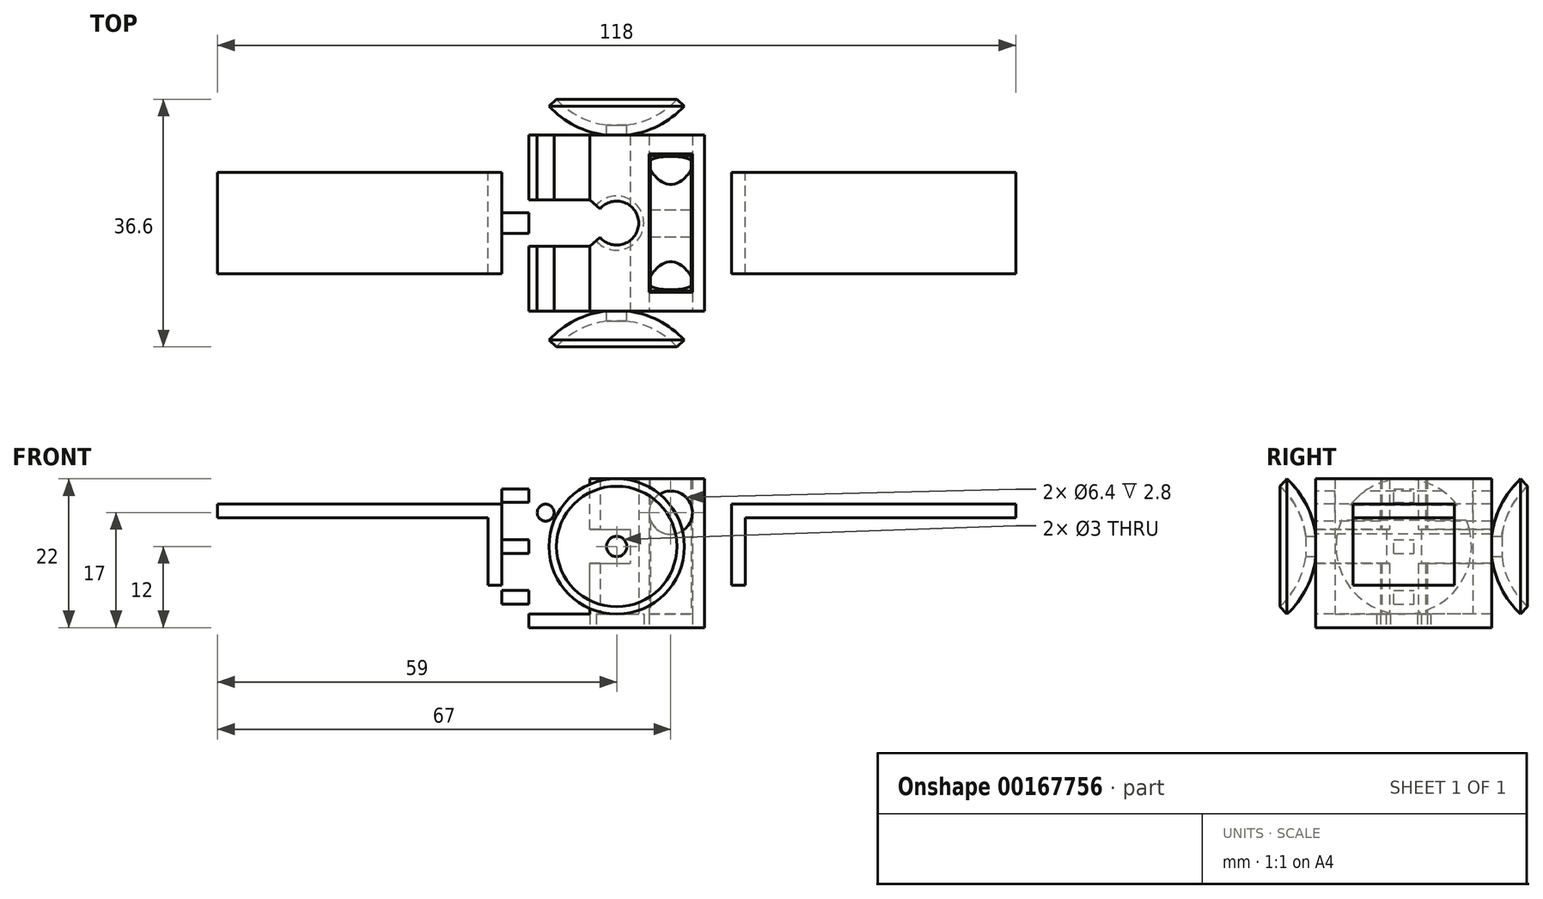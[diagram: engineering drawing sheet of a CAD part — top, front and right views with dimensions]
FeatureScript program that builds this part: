
annotation { "Feature Type Name" : "Feature", "Feature Type Description" : "" }
export const myFeature = defineFeature(function(context is Context, id is Id, definition is map)
    precondition{}
    {
        {
            assignVariable(context, id + "F0", {"name" : "e", "anyValue" : 15});
        }
        {
            var Q0;
            Q0=qCreatedBy(makeId("Front.planeOp"),FACE);
            var sketch = newSketch(context, id + "F1", { "sketchPlane" : qUnion([Q0])});
            skLineSegment(sketch, "E0.bottom", {"start": v(-4, 0) * mm, "end": v(-13, 0) * mm});
            skLineSegment(sketch, "E0.top", {"start": v(-4, 20) * mm, "end": v(-13, 20) * mm});
            skLineSegment(sketch, "E0.left", {"start": v(-4, 0) * mm, "end": v(-4, 20) * mm});
            skLineSegment(sketch, "E0.right", {"start": v(-13, 0) * mm, "end": v(-13, 20) * mm});
            skLineSegment(sketch, "E1.bottom", {"start": v(-4, 6.27) * mm, "end": v(-0.49, 6.27) * mm, "construction": true});
            skLineSegment(sketch, "E1.top", {"start": v(-4, 8.27) * mm, "end": v(-0.49, 8.27) * mm, "construction": true});
            skLineSegment(sketch, "E1.right", {"start": v(-0.49, 6.27) * mm, "end": v(-0.49, 8.27) * mm, "construction": true});
            skLineSegment(sketch, "E2", {"start": v(-4, 0) * mm, "end": v(18.43, 40.1) * mm, "construction": true});
            skLineSegment(sketch, "E3.bottom", {"start": v(-13, 18.5) * mm, "end": v(-17, 18.5) * mm});
            skLineSegment(sketch, "E3.top", {"start": v(-13, 16.5) * mm, "end": v(-17, 16.5) * mm});
            skLineSegment(sketch, "E3.left", {"start": v(-13, 18.5) * mm, "end": v(-13, 16.5) * mm});
            skLineSegment(sketch, "E3.right", {"start": v(-17, 18.5) * mm, "end": v(-17, 16.5) * mm});
            skLineSegment(sketch, "E4.bottom", {"start": v(-13, 11) * mm, "end": v(-17, 11) * mm});
            skLineSegment(sketch, "E4.top", {"start": v(-13, 9) * mm, "end": v(-17, 9) * mm});
            skLineSegment(sketch, "E4.left", {"start": v(-13, 11) * mm, "end": v(-13, 9) * mm});
            skLineSegment(sketch, "E4.right", {"start": v(-17, 11) * mm, "end": v(-17, 9) * mm});
            skLineSegment(sketch, "E5.bottom", {"start": v(-13, 1.5) * mm, "end": v(-17, 1.5) * mm});
            skLineSegment(sketch, "E5.top", {"start": v(-13, 3.5) * mm, "end": v(-17, 3.5) * mm});
            skLineSegment(sketch, "E5.left", {"start": v(-13, 1.5) * mm, "end": v(-13, 3.5) * mm});
            skLineSegment(sketch, "E5.right", {"start": v(-17, 1.5) * mm, "end": v(-17, 3.5) * mm});
            skLineSegment(sketch, "E6", {"start": v(-17, 10) * mm, "end": v(-4, 10) * mm, "construction": true});
            skCircle(sketch, "E7", {"center": v(-10.5, 5) * mm, "radius": 1.25 * mm});
            skLineSegment(sketch, "E8", {"start": v(-10.5, 15) * mm, "end": v(-10.5, 5) * mm, "construction": true});
            skCircle(sketch, "E9.MirrorC", {"center": v(-10.5, 15) * mm, "radius": 1.25 * mm});
            skLineSegment(sketch, "E10.bottom", {"start": v(-3, 0) * mm, "end": v(3, 0) * mm, "construction": true});
            skLineSegment(sketch, "E10.top", {"start": v(-3, 28.23) * mm, "end": v(3, 28.23) * mm, "construction": true});
            skLineSegment(sketch, "E10.left", {"start": v(-3, 0) * mm, "end": v(-3, 28.23) * mm, "construction": true});
            skLineSegment(sketch, "E10.right", {"start": v(3, 0) * mm, "end": v(3, 28.23) * mm, "construction": true});
            skSolve(sketch);
        }
        {
            var Q0;
            {var subQ5=sQuery(id+"F1.wireOp",EDGE,"E0.bottom");Q0=makeQuery(id+"F1.imprint","IMPRINT",FACE,{"disambiguationData":[TD([[makeQuery(id+"F1.imprint","IMPRINT",EDGE,{"derivedFrom":subQ5}),-1.0]])]});}
            extrude(context, id + "F2", {"entities" : qUnion([Q0]), "endBound" : BoundingType.SYMMETRIC, "depth" : 6.5 * mm, "offsetDistance" : 25 * mm});
        }
        {
            var Q0;
            Q0=makeQuery(id+"F1.imprint","IMPRINT",FACE,{"disambiguationData":[TD([[makeQuery(id+"F1.imprint","IMPRINT",EDGE,{"derivedFrom":sQuery(id+"F1.wireOp",EDGE,"E3.bottom")}),1.0]])]});
            var Q1;
            Q1=makeQuery(id+"F1.imprint","IMPRINT",FACE,{"disambiguationData":[TD([[makeQuery(id+"F1.imprint","IMPRINT",EDGE,{"derivedFrom":sQuery(id+"F1.wireOp",EDGE,"E4.bottom")}),1.0]])]});
            var Q2;
            Q2=makeQuery(id+"F1.imprint","IMPRINT",FACE,{"disambiguationData":[TD([[makeQuery(id+"F1.imprint","IMPRINT",EDGE,{"derivedFrom":sQuery(id+"F1.wireOp",EDGE,"E5.bottom")}),-1.0]])]});
            extrude(context, id + "F3", {"entities" : qUnion([Q0, Q1, Q2]), "endBound" : BoundingType.SYMMETRIC, "depth" : 3 * mm, "offsetDistance" : 25 * mm});
        }
        {
            var Q0;
            Q0=qCreatedBy(makeId("Right.planeOp"),FACE);
            var sketch = newSketch(context, id + "F4", { "sketchPlane" : qUnion([Q0])});
            skCircle(sketch, "E11", {"center": v(0, 10) * mm, "radius": 10 * mm});
            skSolve(sketch);
        }
        {
            var Q0;
            Q0 = qSketchRegion(id + "F4", true);
            extrude(context, id + "F5", {"entities" : qUnion([Q0]), "depth" : 11 * mm, "offsetDistance" : 25 * mm, "hasSecondDirection" : true, "secondDirectionOppositeDirection" : true, "secondDirectionDepth" : -5 * mm});
        }
        {
            var Q0;
            Q0=qCreatedBy(makeId("Top.planeOp"),FACE);
            var sketch = newSketch(context, id + "F6", { "sketchPlane" : qUnion([Q0])});
            skLineSegment(sketch, "E12", {"start": v(-13, 3.45) * mm, "end": v(-4, 3.45) * mm});
            skLineSegment(sketch, "E13", {"start": v(4.8, 0) * mm, "end": v(4.8, 10.2) * mm});
            skLineSegment(sketch, "E14", {"start": v(4.8, 10.2) * mm, "end": v(11.2, 10.2) * mm});
            skLineSegment(sketch, "E15", {"start": v(11.2, 10.2) * mm, "end": v(11.2, 0) * mm});
            skLineSegment(sketch, "E16", {"start": v(11.2, 0) * mm, "end": v(13, 0) * mm});
            skLineSegment(sketch, "E17", {"start": v(13, 0) * mm, "end": v(13, 13) * mm});
            skLineSegment(sketch, "E18", {"start": v(13, 13) * mm, "end": v(-13, 13) * mm});
            skLineSegment(sketch, "E19", {"start": v(-13, 13) * mm, "end": v(-13, 3.45) * mm});
            skLineSegment(sketch, "E20.MirrorCS", {"start": v(4.8, 0) * mm, "end": v(4.8, -10.2) * mm});
            skLineSegment(sketch, "E21.MirrorCS", {"start": v(-13, -3.45) * mm, "end": v(-4, -3.45) * mm});
            skLineSegment(sketch, "E22.MirrorCS", {"start": v(4.8, -10.2) * mm, "end": v(11.2, -10.2) * mm});
            skLineSegment(sketch, "E23.MirrorCS", {"start": v(13, 0) * mm, "end": v(13, -13) * mm});
            skLineSegment(sketch, "E24.MirrorCS", {"start": v(13, -13) * mm, "end": v(-13, -13) * mm});
            skLineSegment(sketch, "E25.MirrorCS", {"start": v(-13, -13) * mm, "end": v(-13, -3.45) * mm});
            skLineSegment(sketch, "E26.MirrorCS", {"start": v(11.2, -10.2) * mm, "end": v(11.2, 0) * mm});
            skCircle(sketch, "E27", {"center": v(0, 0) * mm, "radius": 3.25 * mm});
            skLineSegment(sketch, "E28", {"start": v(-4, 3.45) * mm, "end": v(-2.46, 2.12) * mm});
            skLineSegment(sketch, "E29.MirrorCS", {"start": v(-4, -3.45) * mm, "end": v(-2.46, -2.12) * mm});
            skLineSegment(sketch, "E30", {"start": v(13, 13) * mm, "end": v(-13, -13) * mm, "construction": true});
            skSolve(sketch);
        }
        {
            var Q0;
            Q0=makeQuery(id+"F6.imprint","IMPRINT",FACE,{"disambiguationData":[TD([[makeQuery(id+"F6.imprint","IMPRINT",EDGE,{"derivedFrom":sQuery(id+"F6.wireOp",EDGE,"E12")}),1.0]])]});
            var Q1;
            Q1=makeQuery(id+"F2.opExtrude","SWEPT_FACE",FACE,{"disambiguationData":[OSD([sQuery(id+"F1.wireOp",EDGE,"E0.top")])]});
            extrude(context, id + "F7", {"entities" : qUnion([Q0]), "endBound" : BoundingType.UP_TO_SURFACE, "depth" : 25 * mm, "endBoundEntityFace" : qUnion([Q1]), "offsetDistance" : 25 * mm});
        }
        {
            var Q0;
            Q0=makeQuery(id+"F6.imprint","IMPRINT",FACE,{"disambiguationData":[TD([[makeQuery(id+"F6.imprint","IMPRINT",EDGE,{"derivedFrom":sQuery(id+"F6.wireOp",EDGE,"E13")}),-1.0]])]});
            var Q1;
            Q1=makeQuery(id+"F6.imprint","IMPRINT",FACE,{"disambiguationData":[TD([[makeQuery(id+"F6.imprint","IMPRINT",EDGE,{"derivedFrom":sQuery(id+"F6.wireOp",EDGE,"E12")}),1.0]])]});
            extrude(context, id + "F8", {"entities" : qUnion([Q0, Q1]), "operationType" : NewBodyOperationType.ADD, "oppositeDirection" : true, "depth" : 2 * mm, "offsetDistance" : 25 * mm});
        }
        {
            var Q0;
            Q0=makeQuery(id+"F1.imprint","IMPRINT",FACE,{"disambiguationData":[TD([[makeQuery(id+"F1.imprint","IMPRINT",EDGE,{"derivedFrom":sQuery(id+"F1.wireOp",EDGE,"E9.MirrorC")}),-1.0]])]});
            var Q1;
            Q1=makeQuery(id+"F1.imprint","IMPRINT",FACE,{"disambiguationData":[TD([[makeQuery(id+"F1.imprint","IMPRINT",EDGE,{"derivedFrom":sQuery(id+"F1.wireOp",EDGE,"E7")}),1.0]])]});
            var Q2;
            Q2=sQuery(id+"F1.wireOp",EDGE,"E9.MirrorC");
            var Q3;
            Q3=sQuery(id+"F1.wireOp",EDGE,"E7");
            extrude(context, id + "F9", {"entities" : qUnion([Q0, Q1]), "operationType" : NewBodyOperationType.REMOVE, "surfaceEntities" : qUnion([Q2, Q3]), "endBound" : BoundingType.THROUGH_ALL, "oppositeDirection" : true, "depth" : 25 * mm, "offsetDistance" : 25 * mm, "hasSecondDirection" : true, "secondDirectionBound" : SecondDirectionBoundingType.THROUGH_ALL, "secondDirectionOppositeDirection" : false, "secondDirectionDepth" : 25 * mm});
        }
        {
            var Q0;
            {var subQ0=sQuery(id+"F6.wireOp",EDGE,"E24.MirrorCS");Q0=makeQuery(id+"F8.boolean.opBoolean","MERGE",FACE,{"derivedFrom":[makeQuery(id+"F7.opExtrude","SWEPT_FACE",FACE,{"disambiguationData":[OSD([subQ0])]}),makeQuery(id+"F8.opExtrude","SWEPT_FACE",FACE,{"disambiguationData":[OSD([subQ0])]})]});}
            var sketch = newSketch(context, id + "F10", { "sketchPlane" : qUnion([Q0])});
            skLineSegment(sketch, "E31.bottom", {"start": v(-13, 12.5) * mm, "end": v(2, 12.5) * mm});
            skLineSegment(sketch, "E31.top", {"start": v(-13, 7.5) * mm, "end": v(2, 7.5) * mm});
            skLineSegment(sketch, "E31.left", {"start": v(-13, 12.5) * mm, "end": v(-13, 7.5) * mm});
            skLineSegment(sketch, "E31.right", {"start": v(2, 12.5) * mm, "end": v(2, 7.5) * mm});
            skCircle(sketch, "E32", {"center": v(8, 15) * mm, "radius": 3.2 * mm});
            skSolve(sketch);
        }
        {
            var Q0;
            Q0 = qSketchRegion(id + "F10", true);
            extrude(context, id + "F11", {"entities" : qUnion([Q0]), "operationType" : NewBodyOperationType.REMOVE, "endBound" : BoundingType.THROUGH_ALL, "oppositeDirection" : true, "depth" : 25 * mm, "offsetDistance" : 25 * mm});
        }
        {
            var Q0;
            Q0=makeQuery(id+"F8.opExtrude","CAP_FACE",FACE,{"disambiguationData":[OSD([sQuery(id+"F6.wireOp",EDGE,"E12"),sQuery(id+"F6.wireOp",EDGE,"E17"),sQuery(id+"F6.wireOp",EDGE,"E18"),sQuery(id+"F6.wireOp",EDGE,"E19"),sQuery(id+"F6.wireOp",EDGE,"E21.MirrorCS"),sQuery(id+"F6.wireOp",EDGE,"E23.MirrorCS"),sQuery(id+"F6.wireOp",EDGE,"E24.MirrorCS"),sQuery(id+"F6.wireOp",EDGE,"E25.MirrorCS"),sQuery(id+"F6.wireOp",EDGE,"E27"),sQuery(id+"F6.wireOp",EDGE,"E28"),sQuery(id+"F6.wireOp",EDGE,"E29.MirrorCS")])],"isStart":false});
            var sketch = newSketch(context, id + "F12", { "sketchPlane" : qUnion([Q0])});
            skCircle(sketch, "E33", {"center": v(0, 0) * mm, "radius": 4 * mm});
            skSolve(sketch);
        }
        {
            var Q0;
            Q0 = qSketchRegion(id + "F12", true);
            extrude(context, id + "F13", {"entities" : qUnion([Q0]), "operationType" : NewBodyOperationType.REMOVE, "oppositeDirection" : true, "depth" : 2 * mm, "offsetDistance" : 25 * mm});
        }
        {
            var Q0;
            Q0=qCreatedBy(makeId("Right.planeOp"),FACE);
            var sketch = newSketch(context, id + "F14", { "sketchPlane" : qUnion([Q0])});
            skLineSegment(sketch, "E34", {"start": v(0, 10) * mm, "end": v(-26.54, 10) * mm, "construction": true});
            skLineSegment(sketch, "E35", {"start": v(-13, 11.5) * mm, "end": v(-14.5, 11.5) * mm});
            skArc(sketch, "E36", {"start": v(-13, 11.5) * mm, "mid": v(-14.38, 16.14) * mm, "end": v(-17.29, 20) * mm});
            skArc(sketch, "E37", {"start": v(-14.5, 11.5) * mm, "mid": v(-15.75, 15.54) * mm, "end": v(-18.3, 18.9) * mm});
            skLineSegment(sketch, "E38", {"start": v(-17.29, 20) * mm, "end": v(-18.3, 18.9) * mm});
            skLineSegment(sketch, "E39.MirrorCS", {"start": v(13, 11.5) * mm, "end": v(14.5, 11.5) * mm});
            skLineSegment(sketch, "E40.MirrorCS", {"start": v(17.29, 20) * mm, "end": v(18.3, 18.9) * mm});
            skArc(sketch, "E41.MirrorCS", {"start": v(14.5, 11.5) * mm, "mid": v(15.75, 15.54) * mm, "end": v(18.3, 18.9) * mm});
            skArc(sketch, "E42.MirrorCS", {"start": v(13, 11.5) * mm, "mid": v(14.38, 16.14) * mm, "end": v(17.29, 20) * mm});
            skSolve(sketch);
        }
        {
            var Q0;
            Q0=makeQuery(id+"F14.imprint","IMPRINT",FACE,{"disambiguationData":[TD([[makeQuery(id+"F14.imprint","IMPRINT",EDGE,{"derivedFrom":sQuery(id+"F14.wireOp",EDGE,"E35")}),-1.0]])]});
            var Q1;
            Q1=makeQuery(id+"F14.imprint","IMPRINT",FACE,{"disambiguationData":[TD([[makeQuery(id+"F14.imprint","IMPRINT",EDGE,{"derivedFrom":sQuery(id+"F14.wireOp",EDGE,"E39.MirrorCS")}),1.0]])]});
            var Q2;
            Q2=sQuery(id+"F14.wireOp",EDGE,"E34");
            revolve(context, id + "F15", {"entities" : qUnion([Q0, Q1]), "axis" : qUnion([Q2]), "revolveType" : RevolveType.FULL});
        }
        {
            var Q0;
            Q0=qCreatedBy(makeId("Front.planeOp"),FACE);
            var sketch = newSketch(context, id + "F16", { "sketchPlane" : qUnion([Q0])});
            skLineSegment(sketch, "E43.bottom", {"start": v(-17, 16.25) * mm, "end": v(-59, 16.25) * mm});
            skLineSegment(sketch, "E43.top", {"start": v(-17, 14.25) * mm, "end": v(-59, 14.25) * mm});
            skLineSegment(sketch, "E43.left", {"start": v(-17, 16.25) * mm, "end": v(-17, 14.25) * mm});
            skLineSegment(sketch, "E43.right", {"start": v(-59, 16.25) * mm, "end": v(-59, 14.25) * mm});
            skLineSegment(sketch, "E44.MirrorCS", {"start": v(59, 16.25) * mm, "end": v(59, 14.25) * mm});
            skLineSegment(sketch, "E45.MirrorCS", {"start": v(17, 16.25) * mm, "end": v(17, 14.25) * mm});
            skLineSegment(sketch, "E46.MirrorCS", {"start": v(17, 16.25) * mm, "end": v(59, 16.25) * mm});
            skLineSegment(sketch, "E47.MirrorCS", {"start": v(17, 14.25) * mm, "end": v(59, 14.25) * mm});
            skLineSegment(sketch, "E48.bottom", {"start": v(-17, 16.25) * mm, "end": v(-19, 16.25) * mm});
            skLineSegment(sketch, "E48.top", {"start": v(-17, 4.25) * mm, "end": v(-19, 4.25) * mm});
            skLineSegment(sketch, "E48.left", {"start": v(-17, 16.25) * mm, "end": v(-17, 4.25) * mm});
            skLineSegment(sketch, "E48.right", {"start": v(-19, 16.25) * mm, "end": v(-19, 4.25) * mm});
            skLineSegment(sketch, "E49.bottom", {"start": v(17, 16.25) * mm, "end": v(19, 16.25) * mm});
            skLineSegment(sketch, "E49.top", {"start": v(17, 4.25) * mm, "end": v(19, 4.25) * mm});
            skLineSegment(sketch, "E49.left", {"start": v(17, 16.25) * mm, "end": v(17, 4.25) * mm});
            skLineSegment(sketch, "E49.right", {"start": v(19, 16.25) * mm, "end": v(19, 4.25) * mm});
            skSolve(sketch);
        }
        {
            var Q0;
            Q0 = qSketchRegion(id + "F16", true);
            extrude(context, id + "F17", {"entities" : qUnion([Q0]), "endBound" : BoundingType.SYMMETRIC, "depth" : (getVariable(context, 'e')) * mm, "offsetDistance" : 25 * mm});
        }
        {
            var Q0;
            Q0=makeQuery(id+"F8.opExtrude","CAP_FACE",FACE,{"disambiguationData":[OSD([sQuery(id+"F6.wireOp",EDGE,"E12"),sQuery(id+"F6.wireOp",EDGE,"E17"),sQuery(id+"F6.wireOp",EDGE,"E18"),sQuery(id+"F6.wireOp",EDGE,"E19"),sQuery(id+"F6.wireOp",EDGE,"E21.MirrorCS"),sQuery(id+"F6.wireOp",EDGE,"E23.MirrorCS"),sQuery(id+"F6.wireOp",EDGE,"E24.MirrorCS"),sQuery(id+"F6.wireOp",EDGE,"E25.MirrorCS"),sQuery(id+"F6.wireOp",EDGE,"E27"),sQuery(id+"F6.wireOp",EDGE,"E28"),sQuery(id+"F6.wireOp",EDGE,"E29.MirrorCS")])],"isStart":false});
            var sketch = newSketch(context, id + "F18", { "sketchPlane" : qUnion([Q0])});
            skLineSegment(sketch, "E50.bottom", {"start": v(4.8, 2) * mm, "end": v(11.2, 2) * mm});
            skLineSegment(sketch, "E50.top", {"start": v(4.8, -2) * mm, "end": v(11.2, -2) * mm});
            skLineSegment(sketch, "E50.left", {"start": v(4.8, 2) * mm, "end": v(4.8, -2) * mm});
            skLineSegment(sketch, "E50.right", {"start": v(11.2, 2) * mm, "end": v(11.2, -2) * mm});
            skSolve(sketch);
        }
        {
            var Q0;
            Q0=makeQuery(id+"F18.imprint","IMPRINT",FACE,{"disambiguationData":[TD([[makeQuery(id+"F18.imprint","IMPRINT",EDGE,{"derivedFrom":sQuery(id+"F18.wireOp",EDGE,"E50.bottom")}),-1.0]])]});
            var Q1;
            Q1=makeQuery(id+"F8.opExtrude","CAP_FACE",FACE,{"disambiguationData":[OSD([sQuery(id+"F6.wireOp",EDGE,"E12"),sQuery(id+"F6.wireOp",EDGE,"E17"),sQuery(id+"F6.wireOp",EDGE,"E18"),sQuery(id+"F6.wireOp",EDGE,"E19"),sQuery(id+"F6.wireOp",EDGE,"E21.MirrorCS"),sQuery(id+"F6.wireOp",EDGE,"E23.MirrorCS"),sQuery(id+"F6.wireOp",EDGE,"E24.MirrorCS"),sQuery(id+"F6.wireOp",EDGE,"E25.MirrorCS"),sQuery(id+"F6.wireOp",EDGE,"E27"),sQuery(id+"F6.wireOp",EDGE,"E28"),sQuery(id+"F6.wireOp",EDGE,"E29.MirrorCS")])],"isStart":true});
            extrude(context, id + "F19", {"entities" : qUnion([Q0]), "operationType" : NewBodyOperationType.REMOVE, "endBound" : BoundingType.UP_TO_SURFACE, "oppositeDirection" : true, "depth" : 25 * mm, "endBoundEntityFace" : qUnion([Q1]), "offsetDistance" : 25 * mm});
        }
    });
